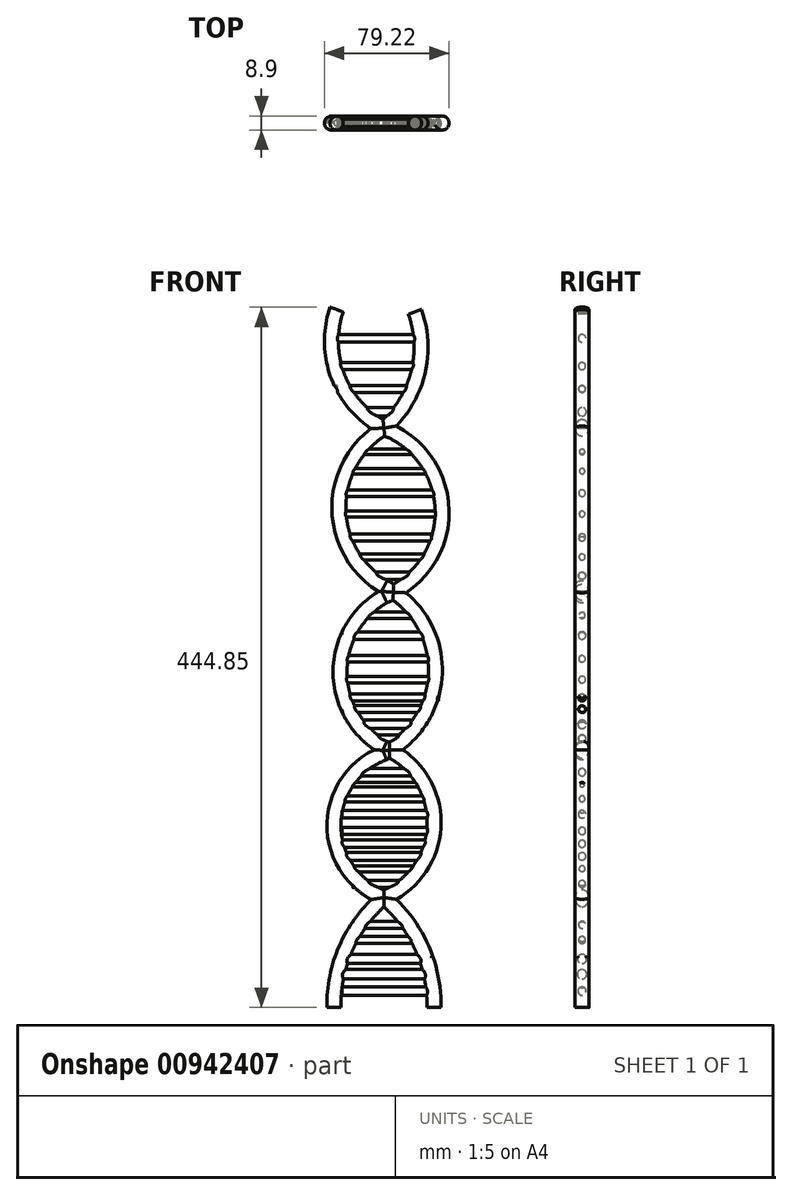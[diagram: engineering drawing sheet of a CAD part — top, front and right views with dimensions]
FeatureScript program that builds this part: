
annotation { "Feature Type Name" : "Feature", "Feature Type Description" : "" }
export const myFeature = defineFeature(function(context is Context, id is Id, definition is map)
    precondition{}
    {
        {
            var Q0;
            Q0=qCreatedBy(makeId("Top.planeOp"),FACE);
            var sketch = newSketch(context, id + "F0", { "sketchPlane" : qUnion([Q0])});
            skCircle(sketch, "E0", {"center": v(-31.75, 0) * mm, "radius": 4.45 * mm});
            skCircle(sketch, "E1", {"center": v(31.75, 0) * mm, "radius": 4.45 * mm});
            skSolve(sketch);
        }
        {
            var Q0;
            Q0=qCreatedBy(makeId("Front.planeOp"),FACE);
            var sketch = newSketch(context, id + "F1", { "sketchPlane" : qUnion([Q0])});
            skArc(sketch, "E2", {"start": v(0, 69.85) * mm, "mid": v(-23.8, 38.53) * mm, "end": v(-31.75, 0) * mm});
            skArc(sketch, "E3", {"start": v(31.75, 0) * mm, "mid": v(23.8, 38.53) * mm, "end": v(0, 69.85) * mm});
            skArc(sketch, "E4", {"start": v(0, 69.85) * mm, "mid": v(31.85, 117.48) * mm, "end": v(0, 165.1) * mm});
            skArc(sketch, "E5", {"start": v(0, 261.14) * mm, "mid": v(-27.88, 213.12) * mm, "end": v(0, 165.1) * mm});
            skArc(sketch, "E6", {"start": v(0, 261.14) * mm, "mid": v(36.94, 314.57) * mm, "end": v(0, 368) * mm});
            skArc(sketch, "E7", {"start": v(-30.06, 443.33) * mm, "mid": v(-28.96, 400.1) * mm, "end": v(0, 368) * mm});
            skArc(sketch, "E8", {"start": v(0, 368) * mm, "mid": v(21.25, 401.9) * mm, "end": v(19.68, 441.87) * mm});
            skArc(sketch, "E9", {"start": v(0, 161.5) * mm, "mid": v(-31.76, 115.68) * mm, "end": v(0, 69.85) * mm});
            skArc(sketch, "E10", {"start": v(0, 161.5) * mm, "mid": v(32.7, 214.4) * mm, "end": v(0, 267.3) * mm});
            skArc(sketch, "E11", {"start": v(0, 368) * mm, "mid": v(-28.64, 317.65) * mm, "end": v(0, 267.3) * mm});
            skSolve(sketch);
        }
        {
            var Q0;
            Q0=makeQuery(id+"F0.imprint","IMPRINT",FACE,{"disambiguationData":[TD([[makeQuery(id+"F0.imprint","IMPRINT",EDGE,{"derivedFrom":sQuery(id+"F0.wireOp",EDGE,"E0")}),1.0]])]});
            var Q1;
            Q1=sQuery(id+"F1.wireOp",EDGE,"E2");
            var Q2;
            Q2=sQuery(id+"F1.wireOp",EDGE,"E4");
            var Q3;
            Q3=sQuery(id+"F1.wireOp",EDGE,"E5");
            var Q4;
            Q4=sQuery(id+"F1.wireOp",EDGE,"E6");
            var Q5;
            Q5=sQuery(id+"F1.wireOp",EDGE,"E7");
            sweep(context, id + "F2", {"profiles" : qUnion([Q0]), "path" : qUnion([Q1, Q2, Q3, Q4, Q5])});
        }
        {
            var Q0;
            Q0=makeQuery(id+"F0.imprint","IMPRINT",FACE,{"disambiguationData":[TD([[makeQuery(id+"F0.imprint","IMPRINT",EDGE,{"derivedFrom":sQuery(id+"F0.wireOp",EDGE,"E1")}),1.0]])]});
            var Q1;
            Q1=sQuery(id+"F1.wireOp",EDGE,"E3");
            var Q2;
            Q2=sQuery(id+"F1.wireOp",EDGE,"E9");
            var Q3;
            Q3=sQuery(id+"F1.wireOp",EDGE,"E10");
            var Q4;
            Q4=sQuery(id+"F1.wireOp",EDGE,"E11");
            var Q5;
            Q5=sQuery(id+"F1.wireOp",EDGE,"E8");
            sweep(context, id + "F3", {"operationType" : NewBodyOperationType.ADD, "profiles" : qUnion([Q0]), "path" : qUnion([Q1, Q2, Q3, Q4, Q5])});
        }
        {
            var Q0;
            Q0=qCreatedBy(makeId("Right.planeOp"),FACE);
            var sketch = newSketch(context, id + "F4", { "sketchPlane" : qUnion([Q0])});
            skCircle(sketch, "E12", {"center": v(0, 10.38) * mm, "radius": 2.63 * mm});
            skCircle(sketch, "E13", {"center": v(0, 21.05) * mm, "radius": 3.02 * mm});
            skCircle(sketch, "E14", {"center": v(0, 30.83) * mm, "radius": 2.94 * mm});
            skCircle(sketch, "E15", {"center": v(0, 42.85) * mm, "radius": 2.25 * mm});
            skCircle(sketch, "E16", {"center": v(0, 52.48) * mm, "radius": 2.24 * mm});
            skCircle(sketch, "E17", {"center": v(0, 78.46) * mm, "radius": 2.21 * mm});
            skCircle(sketch, "E18", {"center": v(0, 88.15) * mm, "radius": 1.87 * mm});
            skCircle(sketch, "E19", {"center": v(0, 96) * mm, "radius": 2.42 * mm});
            skCircle(sketch, "E20", {"center": v(0, 104) * mm, "radius": 2.3 * mm});
            skCircle(sketch, "E21", {"center": v(0, 112.11) * mm, "radius": 2.3 * mm});
            skCircle(sketch, "E22", {"center": v(0, 122.72) * mm, "radius": 2.42 * mm});
            skCircle(sketch, "E23", {"center": v(0, 132.54) * mm, "radius": 1.85 * mm});
            skCircle(sketch, "E24", {"center": v(0, 141.58) * mm, "radius": 1.5 * mm});
            skCircle(sketch, "E25", {"center": v(0, 149.43) * mm, "radius": 2.34 * mm});
            skCircle(sketch, "E26", {"center": v(0, 170.9) * mm, "radius": 2.3 * mm});
            skCircle(sketch, "E27", {"center": v(0, 179.81) * mm, "radius": 2.69 * mm});
            skCircle(sketch, "E28", {"center": v(0, 189.5) * mm, "radius": 2.23 * mm});
            skCircle(sketch, "E29", {"center": v(0, 196.84) * mm, "radius": 2.22 * mm});
            skCircle(sketch, "E30", {"center": v(0, 208.23) * mm, "radius": 2.14 * mm});
            skCircle(sketch, "E31", {"center": v(0, 221.46) * mm, "radius": 2.12 * mm});
            skCircle(sketch, "E32", {"center": v(0, 236.25) * mm, "radius": 2.4 * mm});
            skCircle(sketch, "E33", {"center": v(0, 249.09) * mm, "radius": 1.98 * mm});
            skCircle(sketch, "E34", {"center": v(0, 274.23) * mm, "radius": 2.32 * mm});
            skCircle(sketch, "E35", {"center": v(0, 286.14) * mm, "radius": 1.95 * mm});
            skCircle(sketch, "E36", {"center": v(0, 298.58) * mm, "radius": 2.22 * mm});
            skCircle(sketch, "E37", {"center": v(0, 313.38) * mm, "radius": 1.85 * mm});
            skCircle(sketch, "E38", {"center": v(0, 326.74) * mm, "radius": 2.1 * mm});
            skCircle(sketch, "E39", {"center": v(0, 340.62) * mm, "radius": 1.72 * mm});
            skCircle(sketch, "E40", {"center": v(0, 352.93) * mm, "radius": 1.74 * mm});
            skCircle(sketch, "E41", {"center": v(0, 378.33) * mm, "radius": 2.7 * mm});
            skCircle(sketch, "E42", {"center": v(0, 392.87) * mm, "radius": 2.16 * mm});
            skCircle(sketch, "E43", {"center": v(0, 407.4) * mm, "radius": 2.27 * mm});
            skCircle(sketch, "E44", {"center": v(0, 425.08) * mm, "radius": 2.41 * mm});
            skSolve(sketch);
        }
        {
            var Q0;
            Q0=makeQuery(id+"F4.imprint","IMPRINT",FACE,{"disambiguationData":[TD([[makeQuery(id+"F4.imprint","IMPRINT",EDGE,{"derivedFrom":sQuery(id+"F4.wireOp",EDGE,"E12")}),1.0]])]});
            var Q1;
            Q1=makeQuery(id+"F4.imprint","IMPRINT",FACE,{"disambiguationData":[TD([[makeQuery(id+"F4.imprint","IMPRINT",EDGE,{"derivedFrom":sQuery(id+"F4.wireOp",EDGE,"E13")}),1.0]])]});
            var Q2;
            Q2=makeQuery(id+"F4.imprint","IMPRINT",FACE,{"disambiguationData":[TD([[makeQuery(id+"F4.imprint","IMPRINT",EDGE,{"derivedFrom":sQuery(id+"F4.wireOp",EDGE,"E14")}),1.0]])]});
            var Q3;
            Q3=makeQuery(id+"F4.imprint","IMPRINT",FACE,{"disambiguationData":[TD([[makeQuery(id+"F4.imprint","IMPRINT",EDGE,{"derivedFrom":sQuery(id+"F4.wireOp",EDGE,"E19")}),1.0]])]});
            var Q4;
            Q4=makeQuery(id+"F4.imprint","IMPRINT",FACE,{"disambiguationData":[TD([[makeQuery(id+"F4.imprint","IMPRINT",EDGE,{"derivedFrom":sQuery(id+"F4.wireOp",EDGE,"E20")}),1.0]])]});
            var Q5;
            Q5=makeQuery(id+"F4.imprint","IMPRINT",FACE,{"disambiguationData":[TD([[makeQuery(id+"F4.imprint","IMPRINT",EDGE,{"derivedFrom":sQuery(id+"F4.wireOp",EDGE,"E21")}),1.0]])]});
            var Q6;
            Q6=makeQuery(id+"F4.imprint","IMPRINT",FACE,{"disambiguationData":[TD([[makeQuery(id+"F4.imprint","IMPRINT",EDGE,{"derivedFrom":sQuery(id+"F4.wireOp",EDGE,"E22")}),1.0]])]});
            var Q7;
            Q7=makeQuery(id+"F4.imprint","IMPRINT",FACE,{"disambiguationData":[TD([[makeQuery(id+"F4.imprint","IMPRINT",EDGE,{"derivedFrom":sQuery(id+"F4.wireOp",EDGE,"E23")}),1.0]])]});
            var Q8;
            Q8=makeQuery(id+"F4.imprint","IMPRINT",FACE,{"disambiguationData":[TD([[makeQuery(id+"F4.imprint","IMPRINT",EDGE,{"derivedFrom":sQuery(id+"F4.wireOp",EDGE,"E24")}),1.0]])]});
            var Q9;
            Q9=makeQuery(id+"F4.imprint","IMPRINT",FACE,{"disambiguationData":[TD([[makeQuery(id+"F4.imprint","IMPRINT",EDGE,{"derivedFrom":sQuery(id+"F4.wireOp",EDGE,"E36")}),1.0]])]});
            var Q10;
            Q10=makeQuery(id+"F4.imprint","IMPRINT",FACE,{"disambiguationData":[TD([[makeQuery(id+"F4.imprint","IMPRINT",EDGE,{"derivedFrom":sQuery(id+"F4.wireOp",EDGE,"E39")}),1.0]])]});
            var Q11;
            Q11=makeQuery(id+"F4.imprint","IMPRINT",FACE,{"disambiguationData":[TD([[makeQuery(id+"F4.imprint","IMPRINT",EDGE,{"derivedFrom":sQuery(id+"F4.wireOp",EDGE,"E32")}),1.0]])]});
            var Q12;
            Q12=makeQuery(id+"F4.imprint","IMPRINT",FACE,{"disambiguationData":[TD([[makeQuery(id+"F4.imprint","IMPRINT",EDGE,{"derivedFrom":sQuery(id+"F4.wireOp",EDGE,"E28")}),1.0]])]});
            extrude(context, id + "F5", {"entities" : qUnion([Q0, Q1, Q2, Q3, Q4, Q5, Q6, Q7, Q8, Q9, Q10, Q11, Q12]), "operationType" : NewBodyOperationType.ADD, "depth" : 30.23 * mm, "offsetDistance" : 25.4 * mm});
        }
        {
            var Q0;
            Q0=makeQuery(id+"F5.opExtrude","CAP_FACE",FACE,{"disambiguationData":[OSD([sQuery(id+"F4.wireOp",EDGE,"E28")])],"isStart":true});
            var Q1;
            Q1=makeQuery(id+"F5.opExtrude","CAP_FACE",FACE,{"disambiguationData":[OSD([sQuery(id+"F4.wireOp",EDGE,"E32")])],"isStart":true});
            var Q2;
            Q2=makeQuery(id+"F5.opExtrude","CAP_FACE",FACE,{"disambiguationData":[OSD([sQuery(id+"F4.wireOp",EDGE,"E24")])],"isStart":true});
            var Q3;
            Q3=makeQuery(id+"F5.opExtrude","CAP_FACE",FACE,{"disambiguationData":[OSD([sQuery(id+"F4.wireOp",EDGE,"E23")])],"isStart":true});
            var Q4;
            Q4=makeQuery(id+"F5.opExtrude","CAP_FACE",FACE,{"disambiguationData":[OSD([sQuery(id+"F4.wireOp",EDGE,"E22")])],"isStart":true});
            var Q5;
            Q5=makeQuery(id+"F5.opExtrude","CAP_FACE",FACE,{"disambiguationData":[OSD([sQuery(id+"F4.wireOp",EDGE,"E21")])],"isStart":true});
            var Q6;
            Q6=makeQuery(id+"F5.opExtrude","CAP_FACE",FACE,{"disambiguationData":[OSD([sQuery(id+"F4.wireOp",EDGE,"E20")])],"isStart":true});
            var Q7;
            Q7=makeQuery(id+"F5.opExtrude","CAP_FACE",FACE,{"disambiguationData":[OSD([sQuery(id+"F4.wireOp",EDGE,"E19")])],"isStart":true});
            var Q8;
            Q8=makeQuery(id+"F5.opExtrude","CAP_FACE",FACE,{"disambiguationData":[OSD([sQuery(id+"F4.wireOp",EDGE,"E36")])],"isStart":true});
            var Q9;
            Q9=makeQuery(id+"F5.opExtrude","CAP_FACE",FACE,{"disambiguationData":[OSD([sQuery(id+"F4.wireOp",EDGE,"E39")])],"isStart":true});
            var Q10;
            Q10=makeQuery(id+"F5.opExtrude","CAP_FACE",FACE,{"disambiguationData":[OSD([sQuery(id+"F4.wireOp",EDGE,"E12")])],"isStart":true});
            var Q11;
            Q11=makeQuery(id+"F5.opExtrude","CAP_FACE",FACE,{"disambiguationData":[OSD([sQuery(id+"F4.wireOp",EDGE,"E13")])],"isStart":true});
            var Q12;
            Q12=makeQuery(id+"F5.opExtrude","CAP_FACE",FACE,{"disambiguationData":[OSD([sQuery(id+"F4.wireOp",EDGE,"E14")])],"isStart":true});
            extrude(context, id + "F6", {"entities" : qUnion([Q0, Q1, Q2, Q3, Q4, Q5, Q6, Q7, Q8, Q9, Q10, Q11, Q12]), "operationType" : NewBodyOperationType.ADD, "depth" : 26.67 * mm, "offsetDistance" : 25.4 * mm});
        }
        {
            var Q0;
            Q0=makeQuery(id+"F4.imprint","IMPRINT",FACE,{"disambiguationData":[TD([[makeQuery(id+"F4.imprint","IMPRINT",EDGE,{"derivedFrom":sQuery(id+"F4.wireOp",EDGE,"E38")}),1.0]])]});
            var Q1;
            Q1=makeQuery(id+"F4.imprint","IMPRINT",FACE,{"disambiguationData":[TD([[makeQuery(id+"F4.imprint","IMPRINT",EDGE,{"derivedFrom":sQuery(id+"F4.wireOp",EDGE,"E37")}),1.0]])]});
            var Q2;
            Q2=makeQuery(id+"F4.imprint","IMPRINT",FACE,{"disambiguationData":[TD([[makeQuery(id+"F4.imprint","IMPRINT",EDGE,{"derivedFrom":sQuery(id+"F4.wireOp",EDGE,"E31")}),1.0]])]});
            var Q3;
            Q3=makeQuery(id+"F4.imprint","IMPRINT",FACE,{"disambiguationData":[TD([[makeQuery(id+"F4.imprint","IMPRINT",EDGE,{"derivedFrom":sQuery(id+"F4.wireOp",EDGE,"E30")}),1.0]])]});
            var Q4;
            Q4=makeQuery(id+"F4.imprint","IMPRINT",FACE,{"disambiguationData":[TD([[makeQuery(id+"F4.imprint","IMPRINT",EDGE,{"derivedFrom":sQuery(id+"F4.wireOp",EDGE,"E29")}),1.0]])]});
            extrude(context, id + "F7", {"entities" : qUnion([Q0, Q1, Q2, Q3, Q4]), "operationType" : NewBodyOperationType.ADD, "oppositeDirection" : true, "depth" : 29.2 * mm, "offsetDistance" : 25.4 * mm});
        }
        {
            var Q0;
            Q0=makeQuery(id+"F4.imprint","IMPRINT",FACE,{"disambiguationData":[TD([[makeQuery(id+"F4.imprint","IMPRINT",EDGE,{"derivedFrom":sQuery(id+"F4.wireOp",EDGE,"E37")}),1.0]])]});
            var Q1;
            Q1=makeQuery(id+"F4.imprint","IMPRINT",FACE,{"disambiguationData":[TD([[makeQuery(id+"F4.imprint","IMPRINT",EDGE,{"derivedFrom":sQuery(id+"F4.wireOp",EDGE,"E38")}),1.0]])]});
            var Q2;
            Q2=makeQuery(id+"F4.imprint","IMPRINT",FACE,{"disambiguationData":[TD([[makeQuery(id+"F4.imprint","IMPRINT",EDGE,{"derivedFrom":sQuery(id+"F4.wireOp",EDGE,"E31")}),1.0]])]});
            var Q3;
            Q3=makeQuery(id+"F4.imprint","IMPRINT",FACE,{"disambiguationData":[TD([[makeQuery(id+"F4.imprint","IMPRINT",EDGE,{"derivedFrom":sQuery(id+"F4.wireOp",EDGE,"E30")}),1.0]])]});
            var Q4;
            Q4=makeQuery(id+"F4.imprint","IMPRINT",FACE,{"disambiguationData":[TD([[makeQuery(id+"F4.imprint","IMPRINT",EDGE,{"derivedFrom":sQuery(id+"F4.wireOp",EDGE,"E29")}),1.0]])]});
            extrude(context, id + "F8", {"entities" : qUnion([Q0, Q1, Q2, Q3, Q4]), "operationType" : NewBodyOperationType.ADD, "depth" : 34.54 * mm, "offsetDistance" : 25.4 * mm});
        }
        {
            var Q0;
            Q0=makeQuery(id+"F4.imprint","IMPRINT",FACE,{"disambiguationData":[TD([[makeQuery(id+"F4.imprint","IMPRINT",EDGE,{"derivedFrom":sQuery(id+"F4.wireOp",EDGE,"E34")}),1.0]])]});
            var Q1;
            Q1=makeQuery(id+"F4.imprint","IMPRINT",FACE,{"disambiguationData":[TD([[makeQuery(id+"F4.imprint","IMPRINT",EDGE,{"derivedFrom":sQuery(id+"F4.wireOp",EDGE,"E40")}),1.0]])]});
            var Q2;
            Q2=makeQuery(id+"F4.imprint","IMPRINT",FACE,{"disambiguationData":[TD([[makeQuery(id+"F4.imprint","IMPRINT",EDGE,{"derivedFrom":sQuery(id+"F4.wireOp",EDGE,"E26")}),1.0]])]});
            var Q3;
            Q3=makeQuery(id+"F4.imprint","IMPRINT",FACE,{"disambiguationData":[TD([[makeQuery(id+"F4.imprint","IMPRINT",EDGE,{"derivedFrom":sQuery(id+"F4.wireOp",EDGE,"E27")}),1.0]])]});
            var Q4;
            Q4=makeQuery(id+"F4.imprint","IMPRINT",FACE,{"disambiguationData":[TD([[makeQuery(id+"F4.imprint","IMPRINT",EDGE,{"derivedFrom":sQuery(id+"F4.wireOp",EDGE,"E33")}),1.0]])]});
            var Q5;
            Q5=makeQuery(id+"F4.imprint","IMPRINT",FACE,{"disambiguationData":[TD([[makeQuery(id+"F4.imprint","IMPRINT",EDGE,{"derivedFrom":sQuery(id+"F4.wireOp",EDGE,"E42")}),1.0]])]});
            var Q6;
            Q6=makeQuery(id+"F4.imprint","IMPRINT",FACE,{"disambiguationData":[TD([[makeQuery(id+"F4.imprint","IMPRINT",EDGE,{"derivedFrom":sQuery(id+"F4.wireOp",EDGE,"E15")}),1.0]])]});
            var Q7;
            Q7=makeQuery(id+"F4.imprint","IMPRINT",FACE,{"disambiguationData":[TD([[makeQuery(id+"F4.imprint","IMPRINT",EDGE,{"derivedFrom":sQuery(id+"F4.wireOp",EDGE,"E16")}),1.0]])]});
            var Q8;
            Q8=makeQuery(id+"F4.imprint","IMPRINT",FACE,{"disambiguationData":[TD([[makeQuery(id+"F4.imprint","IMPRINT",EDGE,{"derivedFrom":sQuery(id+"F4.wireOp",EDGE,"E17")}),1.0]])]});
            extrude(context, id + "F9", {"entities" : qUnion([Q0, Q1, Q2, Q3, Q4, Q5, Q6, Q7, Q8]), "operationType" : NewBodyOperationType.ADD, "depth" : 17.27 * mm, "offsetDistance" : 25.4 * mm});
        }
        {
            var Q0;
            Q0=makeQuery(id+"F4.imprint","IMPRINT",FACE,{"disambiguationData":[TD([[makeQuery(id+"F4.imprint","IMPRINT",EDGE,{"derivedFrom":sQuery(id+"F4.wireOp",EDGE,"E43")}),1.0]])]});
            var Q1;
            Q1=makeQuery(id+"F4.imprint","IMPRINT",FACE,{"disambiguationData":[TD([[makeQuery(id+"F4.imprint","IMPRINT",EDGE,{"derivedFrom":sQuery(id+"F4.wireOp",EDGE,"E44")}),1.0]])]});
            var Q2;
            Q2=makeQuery(id+"F4.imprint","IMPRINT",FACE,{"disambiguationData":[TD([[makeQuery(id+"F4.imprint","IMPRINT",EDGE,{"derivedFrom":sQuery(id+"F4.wireOp",EDGE,"E25")}),1.0]])]});
            var Q3;
            Q3=makeQuery(id+"F4.imprint","IMPRINT",FACE,{"disambiguationData":[TD([[makeQuery(id+"F4.imprint","IMPRINT",EDGE,{"derivedFrom":sQuery(id+"F4.wireOp",EDGE,"E18")}),1.0]])]});
            extrude(context, id + "F10", {"entities" : qUnion([Q0, Q1, Q2, Q3]), "operationType" : NewBodyOperationType.ADD, "depth" : 23.88 * mm, "offsetDistance" : 25.4 * mm});
        }
        {
            var Q0;
            Q0=makeQuery(id+"F4.imprint","IMPRINT",FACE,{"disambiguationData":[TD([[makeQuery(id+"F4.imprint","IMPRINT",EDGE,{"derivedFrom":sQuery(id+"F4.wireOp",EDGE,"E43")}),1.0]])]});
            var Q1;
            Q1=makeQuery(id+"F4.imprint","IMPRINT",FACE,{"disambiguationData":[TD([[makeQuery(id+"F4.imprint","IMPRINT",EDGE,{"derivedFrom":sQuery(id+"F4.wireOp",EDGE,"E44")}),1.0]])]});
            var Q2;
            Q2=makeQuery(id+"F4.imprint","IMPRINT",FACE,{"disambiguationData":[TD([[makeQuery(id+"F4.imprint","IMPRINT",EDGE,{"derivedFrom":sQuery(id+"F4.wireOp",EDGE,"E42")}),1.0]])]});
            extrude(context, id + "F11", {"entities" : qUnion([Q0, Q1, Q2]), "operationType" : NewBodyOperationType.ADD, "oppositeDirection" : true, "depth" : 32.5 * mm, "offsetDistance" : 25.4 * mm});
        }
        {
            var Q0;
            Q0=makeQuery(id+"F4.imprint","IMPRINT",FACE,{"disambiguationData":[TD([[makeQuery(id+"F4.imprint","IMPRINT",EDGE,{"derivedFrom":sQuery(id+"F4.wireOp",EDGE,"E15")}),1.0]])]});
            var Q1;
            Q1=makeQuery(id+"F4.imprint","IMPRINT",FACE,{"disambiguationData":[TD([[makeQuery(id+"F4.imprint","IMPRINT",EDGE,{"derivedFrom":sQuery(id+"F4.wireOp",EDGE,"E16")}),1.0]])]});
            var Q2;
            Q2=makeQuery(id+"F4.imprint","IMPRINT",FACE,{"disambiguationData":[TD([[makeQuery(id+"F4.imprint","IMPRINT",EDGE,{"derivedFrom":sQuery(id+"F4.wireOp",EDGE,"E17")}),1.0]])]});
            var Q3;
            Q3=makeQuery(id+"F4.imprint","IMPRINT",FACE,{"disambiguationData":[TD([[makeQuery(id+"F4.imprint","IMPRINT",EDGE,{"derivedFrom":sQuery(id+"F4.wireOp",EDGE,"E18")}),1.0]])]});
            var Q4;
            Q4=makeQuery(id+"F4.imprint","IMPRINT",FACE,{"disambiguationData":[TD([[makeQuery(id+"F4.imprint","IMPRINT",EDGE,{"derivedFrom":sQuery(id+"F4.wireOp",EDGE,"E25")}),1.0]])]});
            var Q5;
            Q5=makeQuery(id+"F4.imprint","IMPRINT",FACE,{"disambiguationData":[TD([[makeQuery(id+"F4.imprint","IMPRINT",EDGE,{"derivedFrom":sQuery(id+"F4.wireOp",EDGE,"E35")}),1.0]])]});
            var Q6;
            Q6=makeQuery(id+"F4.imprint","IMPRINT",FACE,{"disambiguationData":[TD([[makeQuery(id+"F4.imprint","IMPRINT",EDGE,{"derivedFrom":sQuery(id+"F4.wireOp",EDGE,"E40")}),1.0]])]});
            extrude(context, id + "F12", {"entities" : qUnion([Q0, Q1, Q2, Q3, Q4, Q5, Q6]), "operationType" : NewBodyOperationType.ADD, "oppositeDirection" : true, "depth" : 19.8 * mm, "offsetDistance" : 25.4 * mm});
        }
        {
            var Q0;
            Q0=makeQuery(id+"F4.imprint","IMPRINT",FACE,{"disambiguationData":[TD([[makeQuery(id+"F4.imprint","IMPRINT",EDGE,{"derivedFrom":sQuery(id+"F4.wireOp",EDGE,"E27")}),1.0]])]});
            var Q1;
            Q1=makeQuery(id+"F4.imprint","IMPRINT",FACE,{"disambiguationData":[TD([[makeQuery(id+"F4.imprint","IMPRINT",EDGE,{"derivedFrom":sQuery(id+"F4.wireOp",EDGE,"E26")}),1.0]])]});
            var Q2;
            Q2=makeQuery(id+"F4.imprint","IMPRINT",FACE,{"disambiguationData":[TD([[makeQuery(id+"F4.imprint","IMPRINT",EDGE,{"derivedFrom":sQuery(id+"F4.wireOp",EDGE,"E33")}),1.0]])]});
            var Q3;
            Q3=makeQuery(id+"F4.imprint","IMPRINT",FACE,{"disambiguationData":[TD([[makeQuery(id+"F4.imprint","IMPRINT",EDGE,{"derivedFrom":sQuery(id+"F4.wireOp",EDGE,"E41")}),1.0]])]});
            extrude(context, id + "F13", {"entities" : qUnion([Q0, Q1, Q2, Q3]), "operationType" : NewBodyOperationType.ADD, "oppositeDirection" : true, "depth" : 12.75 * mm, "offsetDistance" : 25.4 * mm});
        }
        {
            var Q0;
            Q0=makeQuery(id+"F11.opExtrude","CAP_FACE",FACE,{"disambiguationData":[OSD([sQuery(id+"F4.wireOp",EDGE,"E42")])],"isStart":false});
            extrude(context, id + "F14", {"entities" : qUnion([Q0]), "operationType" : NewBodyOperationType.REMOVE, "oppositeDirection" : true, "depth" : 2.95 * mm, "offsetDistance" : 25.4 * mm});
        }
        {
            var Q0;
            Q0=makeQuery(id+"F4.imprint","IMPRINT",FACE,{"disambiguationData":[TD([[makeQuery(id+"F4.imprint","IMPRINT",EDGE,{"derivedFrom":sQuery(id+"F4.wireOp",EDGE,"E35")}),1.0]])]});
            extrude(context, id + "F15", {"entities" : qUnion([Q0]), "operationType" : NewBodyOperationType.ADD, "depth" : 30.99 * mm, "offsetDistance" : 25.4 * mm});
        }
        {
            var Q0;
            Q0=makeQuery(id+"F4.imprint","IMPRINT",FACE,{"disambiguationData":[TD([[makeQuery(id+"F4.imprint","IMPRINT",EDGE,{"derivedFrom":sQuery(id+"F4.wireOp",EDGE,"E41")}),1.0]])]});
            extrude(context, id + "F16", {"entities" : qUnion([Q0]), "operationType" : NewBodyOperationType.ADD, "depth" : 8.13 * mm, "offsetDistance" : 25.4 * mm});
        }
        {
            var Q0;
            Q0=makeQuery(id+"F4.imprint","IMPRINT",FACE,{"disambiguationData":[TD([[makeQuery(id+"F4.imprint","IMPRINT",EDGE,{"derivedFrom":sQuery(id+"F4.wireOp",EDGE,"E34")}),1.0]])]});
            extrude(context, id + "F17", {"entities" : qUnion([Q0]), "operationType" : NewBodyOperationType.ADD, "oppositeDirection" : true, "depth" : 11.43 * mm, "offsetDistance" : 25.4 * mm});
        }
    });
